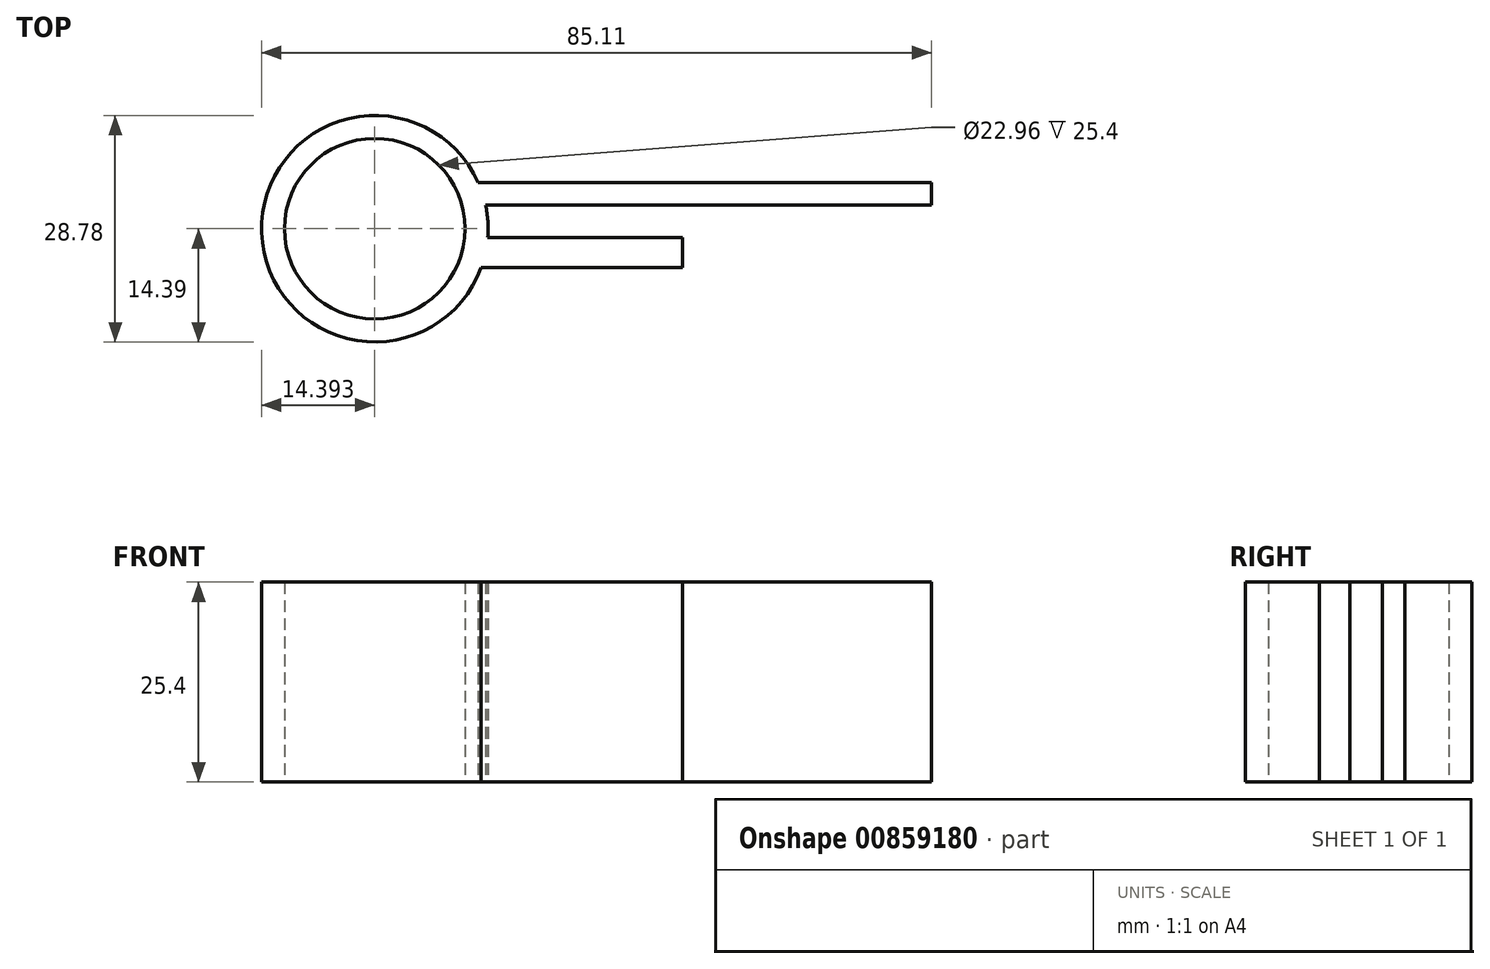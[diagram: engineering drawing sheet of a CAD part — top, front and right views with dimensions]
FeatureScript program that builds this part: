
annotation { "Feature Type Name" : "Feature", "Feature Type Description" : "" }
export const myFeature = defineFeature(function(context is Context, id is Id, definition is map)
    precondition{}
    {
        {
            var Q0;
            Q0=qCreatedBy(makeId("Top.planeOp"),FACE);
            var sketch = newSketch(context, id + "F0", { "sketchPlane" : qUnion([Q0])});
            skCircle(sketch, "E0", {"center": v(-41.62, 6.92) * mm, "radius": 11.48 * mm});
            skCircle(sketch, "E1", {"center": v(-41.62, 6.92) * mm, "radius": 14.39 * mm});
            skLineSegment(sketch, "E2.bottom", {"start": v(-28.49, 12.8) * mm, "end": v(29.1, 12.8) * mm});
            skLineSegment(sketch, "E2.top", {"start": v(-28.49, 9.95) * mm, "end": v(29.1, 9.95) * mm});
            skLineSegment(sketch, "E2.left", {"start": v(-28.49, 12.8) * mm, "end": v(-28.49, 9.95) * mm});
            skLineSegment(sketch, "E2.right", {"start": v(29.1, 12.8) * mm, "end": v(29.1, 9.95) * mm});
            skLineSegment(sketch, "E3.bottom", {"start": v(-28.1, 1.97) * mm, "end": v(-2.56, 1.97) * mm});
            skLineSegment(sketch, "E3.top", {"start": v(-28.1, 5.78) * mm, "end": v(-2.56, 5.78) * mm});
            skLineSegment(sketch, "E3.left", {"start": v(-28.1, 1.97) * mm, "end": v(-28.1, 5.78) * mm});
            skLineSegment(sketch, "E3.right", {"start": v(-2.56, 1.97) * mm, "end": v(-2.56, 5.78) * mm});
            skSolve(sketch);
        }
        {
            var Q0;
            {var subQ0=sQuery(id+"F0.wireOp",EDGE,"E2.left");Q0=makeQuery(id+"F0.imprint","IMPRINT",FACE,{"disambiguationData":[TD([[makeQuery(id+"F0.imprint","IMPRINT",EDGE,{"derivedFrom":subQ0}),1.0]])]});}
            var Q1;
            {var subQ0=sQuery(id+"F0.wireOp",EDGE,"E3.left");Q1=makeQuery(id+"F0.imprint","IMPRINT",FACE,{"disambiguationData":[TD([[makeQuery(id+"F0.imprint","IMPRINT",EDGE,{"derivedFrom":subQ0}),-1.0]])]});}
            var Q2;
            {var subQ0=sQuery(id+"F0.wireOp",EDGE,"E3.bottom");Q2=makeQuery(id+"F0.imprint","IMPRINT",FACE,{"disambiguationData":[TD([[makeQuery(id+"F0.imprint","IMPRINT",EDGE,{"derivedFrom":subQ0}),1.0]])]});}
            var Q3;
            {var subQ0=sQuery(id+"F0.wireOp",EDGE,"E2.bottom");Q3=makeQuery(id+"F0.imprint","IMPRINT",FACE,{"disambiguationData":[TD([[makeQuery(id+"F0.imprint","IMPRINT",EDGE,{"derivedFrom":subQ0}),-1.0]])]});}
            var Q4;
            Q4=makeQuery(id+"F0.imprint","IMPRINT",FACE,{"disambiguationData":[TD([[makeQuery(id+"F0.imprint","IMPRINT",EDGE,{"derivedFrom":sQuery(id+"F0.wireOp",EDGE,"E0")}),-1.0]])]});
            extrude(context, id + "F1", {"entities" : qUnion([Q0, Q1, Q2, Q3, Q4]), "depth" : 25.4 * mm, "offsetDistance" : 25.4 * mm});
        }
    });
